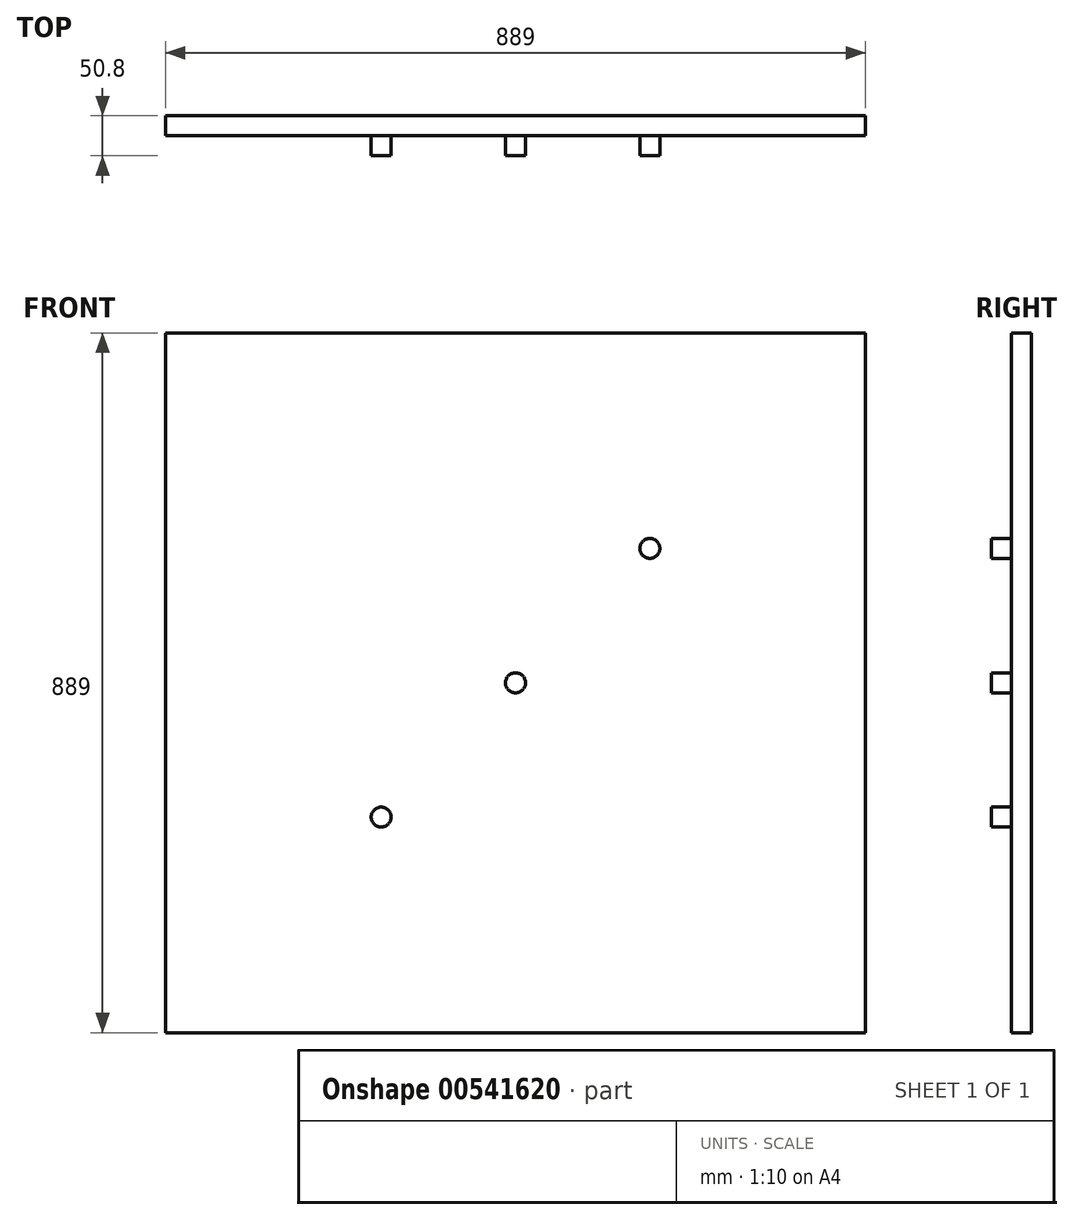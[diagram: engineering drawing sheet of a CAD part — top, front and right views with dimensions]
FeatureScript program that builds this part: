
annotation { "Feature Type Name" : "Feature", "Feature Type Description" : "" }
export const myFeature = defineFeature(function(context is Context, id is Id, definition is map)
    precondition{}
    {
        {
            var Q0;
            Q0=qCreatedBy(makeId("Front.planeOp"),FACE);
            var sketch = newSketch(context, id + "F0", { "sketchPlane" : qUnion([Q0])});
            skLineSegment(sketch, "E0.bottom", {"start": v(444.5, 444.5) * mm, "end": v(-444.5, 444.5) * mm});
            skLineSegment(sketch, "E0.top", {"start": v(444.5, -444.5) * mm, "end": v(-444.5, -444.5) * mm});
            skLineSegment(sketch, "E0.left", {"start": v(444.5, 444.5) * mm, "end": v(444.5, -444.5) * mm});
            skLineSegment(sketch, "E0.right", {"start": v(-444.5, 444.5) * mm, "end": v(-444.5, -444.5) * mm});
            skPoint(sketch, "E0.middle", {"position": v(0, 0) * mm});
            skSolve(sketch);
        }
        {
            var Q0;
            Q0 = qSketchRegion(id + "F0", true);
            extrude(context, id + "F1", {"entities" : qUnion([Q0]), "endBound" : BoundingType.SYMMETRIC, "depth" : 25.4 * mm, "offsetDistance" : 25.4 * mm});
        }
        {
            var Q0;
            Q0=makeQuery(id+"F1.opExtrude","CAP_FACE",FACE,{"disambiguationData":[OSD([sQuery(id+"F0.wireOp",EDGE,"E0.bottom"),sQuery(id+"F0.wireOp",EDGE,"E0.top"),sQuery(id+"F0.wireOp",EDGE,"E0.left"),sQuery(id+"F0.wireOp",EDGE,"E0.right")])],"isStart":false});
            var sketch = newSketch(context, id + "F2", { "sketchPlane" : qUnion([Q0])});
            skLineSegment(sketch, "E1", {"start": v(0, 0) * mm, "end": v(-170.62, -170.62) * mm});
            skLineSegment(sketch, "E2", {"start": v(0, 0) * mm, "end": v(170.62, 170.62) * mm});
            skCircle(sketch, "E3", {"center": v(-170.62, -170.62) * mm, "radius": 12.7 * mm});
            skCircle(sketch, "E4", {"center": v(0, 0) * mm, "radius": 12.7 * mm});
            skCircle(sketch, "E5", {"center": v(170.62, 170.62) * mm, "radius": 12.7 * mm});
            skSolve(sketch);
        }
        {
            var Q0;
            Q0 = qSketchRegion(id + "F2", true);
            extrude(context, id + "F3", {"entities" : qUnion([Q0]), "operationType" : NewBodyOperationType.ADD, "depth" : 25.4 * mm, "offsetDistance" : 25.4 * mm});
        }
    });
